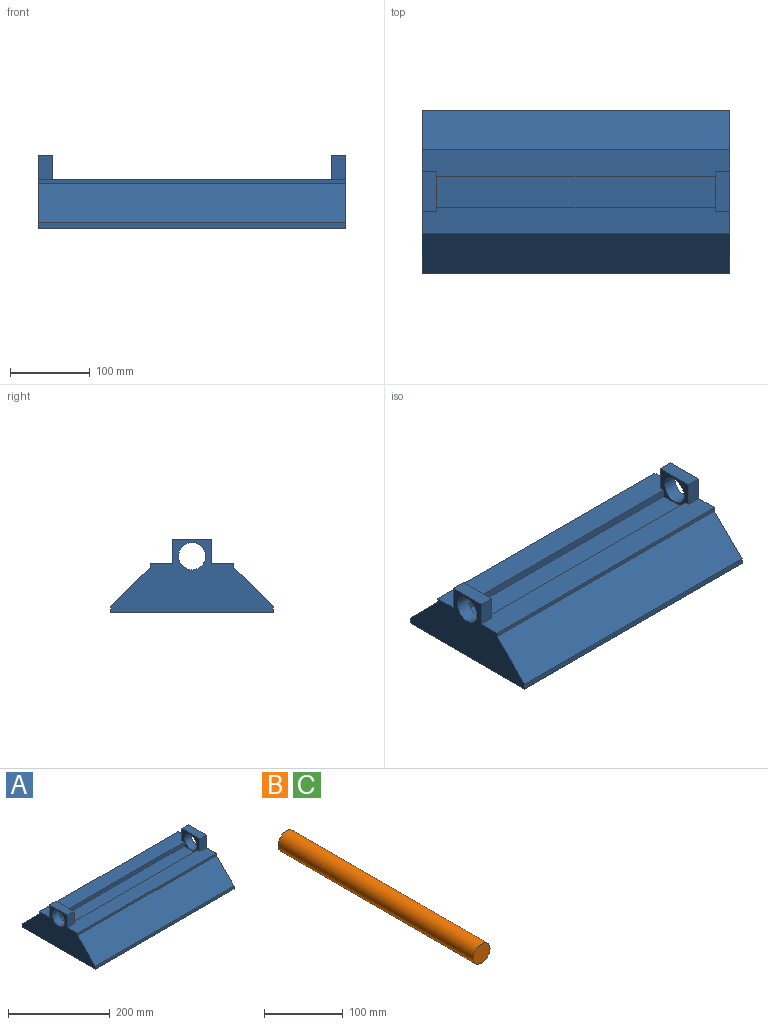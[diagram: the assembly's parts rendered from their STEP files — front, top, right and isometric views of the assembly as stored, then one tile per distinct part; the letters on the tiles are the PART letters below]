
ASSEMBLY  parts=3 mates=2
PART A: 29 faces, bbox 386x203.7x91.8 mm
  f0: plane 350x10mm, normal (0,-1,0), area 3500mm2, adj f1,f7,f21,f22
  f1: plane 350x38mm, normal (0,0,1), area 13300mm2, adj f0,f2,f21,f22
  f2: plane 350x10mm, normal (0,1,0), area 3500mm2, adj f1,f3,f21,f22
  f3: plane 386x33.73mm, normal (0,0,1), area 12803mm2, adj f2,f4,f16,f20,f21,f22,f25,f27
  f4: plane 386x5.27mm, normal (0,-1,0), area 2035mm2, adj f3,f11,f20,f27
  f5: plane 350x80mm, normal (0,0,-1), area 28000mm2, adj f10,f14,f15,f28
  f6: plane 386x5.27mm, normal (0,1,0), area 2035mm2, adj f7,f13,f20,f27
  f7: plane 386x33.73mm, normal (0,0,1), area 12803mm2, adj f0,f6,f18,f20,f21,f22,f23,f27
  f8: plane 386x7.46mm, normal (0,-1,0), area 2878mm2, adj f9,f11,f20,f27
  f9: plane 386x203.68mm, normal (0,0,-1), area 19932.5mm2, adj f8,f10,f12,f14,f15,f20,f27,f28
  f10: plane 350x43.84mm, normal (0,0.71,-0.71), area 21700mm2, adj f5,f9,f15,f28
  f11: plane 386x49.11mm, normal (0,-0.71,0.71), area 26810mm2, adj f4,f8,f20,f27
  f12: plane 386x7.46mm, normal (0,1,0), area 2878mm2, adj f9,f13,f20,f27
  f13: plane 386x49.11mm, normal (0,0.71,0.71), area 26810mm2, adj f6,f12,f20,f27
  f14: plane 350x43.84mm, normal (0,-0.71,-0.71), area 21700mm2, adj f5,f9,f15,f28
  f15: plane 167.68x43.84mm, normal (1,0,0), area 5429.2mm2, adj f5,f9,f10,f14
  f16: plane 30x18mm, normal (0,-1,0), area 540mm2, adj f3,f17,f20,f21
  f17: plane 50x18mm, normal (0,0,1), area 900mm2, adj f16,f18,f20,f21
  f18: plane 30x18mm, normal (0,1,0), area 540mm2, adj f7,f17,f20,f21
  f19: cylinder r=17mm len=34mm, axis (1,0,0), area 1922.7mm2, adj f20,f21
  f20: plane 203.68x91.84mm, normal (-1,0,0), area 10257.9mm2, adj f3,f4,f6,f7,f8,f9,f11,f12
  f21: plane 50x40mm, normal (1,0,0), area 972.1mm2, adj f0,f1,f2,f3,f7,f16,f17,f18
  f22: plane 50x40mm, normal (-1,0,0), area 972.1mm2, adj f0,f1,f2,f3,f7,f23,f24,f25
  f23: plane 30x18mm, normal (0,1,0), area 540mm2, adj f7,f22,f24,f27
  f24: plane 50x18mm, normal (0,0,1), area 900mm2, adj f22,f23,f25,f27
  f25: plane 30x18mm, normal (0,-1,0), area 540mm2, adj f3,f22,f24,f27
  f26: cylinder r=17mm len=34mm, axis (-1,0,0), area 1922.7mm2, adj f22,f27
  f27: plane 203.68x91.84mm, normal (1,0,0), area 10257.9mm2, adj f3,f4,f6,f7,f8,f9,f11,f12
  f28: plane 167.68x43.84mm, normal (-1,0,0), area 5429.2mm2, adj f5,f9,f10,f14
PART B: 3 faces, bbox 30x350x30 mm
  f0: cylinder r=15mm len=350mm, axis (0,1,0), area 32986.7mm2, adj f1,f2
  f1: plane 30x30mm, normal (0,-1,0), area 706.9mm2, adj f0
  f2: plane 30x30mm, normal (0,1,0), area 706.9mm2, adj f0
PART C: same geometry as B
PLACE A t=(269.86,145.85,-17.01)mm
PLACE B rot(axis=(0.58,0.58,-0.58),120deg) t=(269.86,165.85,-41.52)mm
PLACE C rot(axis=(0,0,-1),90deg) t=(269.86,125.85,-41.52)mm
MATE fastened B.f0 <-> A.f15  axis (-1,0,0) through (94.86,165.85,-41.52)mm
MATE fastened C.f0 <-> A.f28  axis (1,0,0) through (444.86,125.85,-41.52)mm
